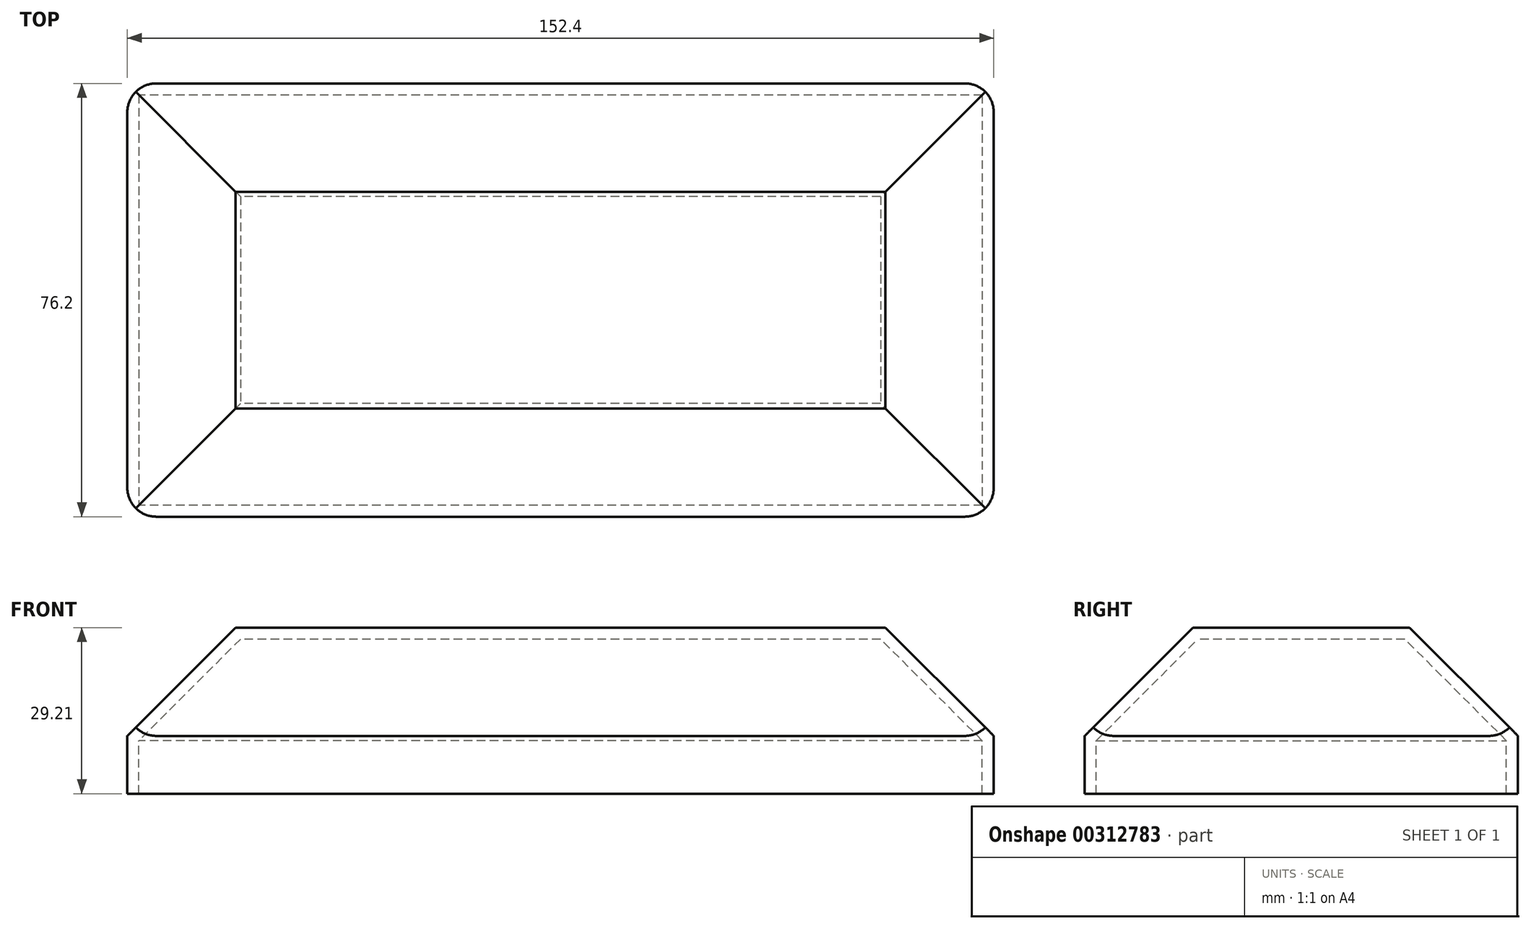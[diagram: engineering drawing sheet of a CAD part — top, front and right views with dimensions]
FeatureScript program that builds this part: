
annotation { "Feature Type Name" : "Feature", "Feature Type Description" : "" }
export const myFeature = defineFeature(function(context is Context, id is Id, definition is map)
    precondition{}
    {
        {
            var Q0;
            Q0=qCreatedBy(makeId("Top.planeOp"),FACE);
            var sketch = newSketch(context, id + "F0", { "sketchPlane" : qUnion([Q0])});
            skLineSegment(sketch, "E0.bottom", {"start": v(0, 0) * mm, "end": v(-152.4, 0) * mm});
            skLineSegment(sketch, "E0.top", {"start": v(0, -76.2) * mm, "end": v(-152.4, -76.2) * mm});
            skLineSegment(sketch, "E0.left", {"start": v(0, 0) * mm, "end": v(0, -76.2) * mm});
            skLineSegment(sketch, "E0.right", {"start": v(-152.4, 0) * mm, "end": v(-152.4, -76.2) * mm});
            skSolve(sketch);
        }
        {
            var Q0;
            Q0=makeQuery(id+"F0.imprint","IMPRINT",FACE,{"disambiguationData":[TD([[makeQuery(id+"F0.imprint","IMPRINT",EDGE,{"derivedFrom":sQuery(id+"F0.wireOp",EDGE,"E0.bottom")}),1.0]])]});
            extrude(context, id + "F1", {"entities" : qUnion([Q0]), "depth" : 19.05 * mm});
        }
        {
            var Q0;
            Q0=makeQuery(id+"F1.opExtrude","CAP_FACE",FACE,{"disambiguationData":[OSD([sQuery(id+"F0.wireOp",EDGE,"E0.bottom"),sQuery(id+"F0.wireOp",EDGE,"E0.top"),sQuery(id+"F0.wireOp",EDGE,"E0.left"),sQuery(id+"F0.wireOp",EDGE,"E0.right")])],"isStart":false});
            chamfer(context, id + "F2", {"entities" : qUnion([Q0]), "width" : 19.05 * mm, "tangentPropagation" : true});
        }
        {
            var Q0;
            Q0=makeQuery(id+"F1.opExtrude","CAP_FACE",FACE,{"disambiguationData":[OSD([sQuery(id+"F0.wireOp",EDGE,"E0.bottom"),sQuery(id+"F0.wireOp",EDGE,"E0.top"),sQuery(id+"F0.wireOp",EDGE,"E0.left"),sQuery(id+"F0.wireOp",EDGE,"E0.right")])],"isStart":true});
            var sketch = newSketch(context, id + "F3", { "sketchPlane" : qUnion([Q0])});
            skLineSegment(sketch, "E1.bottom", {"start": v(0, 0) * mm, "end": v(-152.4, 0) * mm});
            skLineSegment(sketch, "E1.top", {"start": v(0, 76.2) * mm, "end": v(-152.4, 76.2) * mm});
            skLineSegment(sketch, "E1.left", {"start": v(0, 0) * mm, "end": v(0, 76.2) * mm});
            skLineSegment(sketch, "E1.right", {"start": v(-152.4, 0) * mm, "end": v(-152.4, 76.2) * mm});
            skSolve(sketch);
        }
        {
            var Q0;
            Q0=makeQuery(id+"F3.imprint","IMPRINT",FACE,{"disambiguationData":[TD([[makeQuery(id+"F3.imprint","IMPRINT",EDGE,{"derivedFrom":sQuery(id+"F3.wireOp",EDGE,"E1.bottom")}),-1.0]])]});
            extrude(context, id + "F4", {"entities" : qUnion([Q0]), "operationType" : NewBodyOperationType.ADD, "depth" : 10.16 * mm});
        }
        {
            var Q0;
            Q0=makeQuery(id+"F4.opExtrude","CAP_FACE",FACE,{"disambiguationData":[OSD([sQuery(id+"F3.wireOp",EDGE,"E1.bottom"),sQuery(id+"F3.wireOp",EDGE,"E1.top"),sQuery(id+"F3.wireOp",EDGE,"E1.left"),sQuery(id+"F3.wireOp",EDGE,"E1.right")])],"isStart":false});
            shell(context, id + "F5", {"entities" : qUnion([Q0]), "thickness" : 2.03 * mm});
        }
        {
            var Q0;
            Q0=makeQuery(id+"F4.opExtrude","SWEPT_EDGE",EDGE,{"disambiguationData":[OSD([sQuery(id+"F3.wireOp",EDGE,"E1.bottom"),sQuery(id+"F3.wireOp",EDGE,"E1.left")])]});
            var Q1;
            Q1=makeQuery(id+"F4.opExtrude","SWEPT_EDGE",EDGE,{"disambiguationData":[OSD([sQuery(id+"F3.wireOp",EDGE,"E1.bottom"),sQuery(id+"F3.wireOp",EDGE,"E1.right")])]});
            var Q2;
            Q2=makeQuery(id+"F4.opExtrude","SWEPT_EDGE",EDGE,{"disambiguationData":[OSD([sQuery(id+"F3.wireOp",EDGE,"E1.top"),sQuery(id+"F3.wireOp",EDGE,"E1.right")])]});
            var Q3;
            Q3=makeQuery(id+"F4.opExtrude","SWEPT_EDGE",EDGE,{"disambiguationData":[OSD([sQuery(id+"F3.wireOp",EDGE,"E1.top"),sQuery(id+"F3.wireOp",EDGE,"E1.left")])]});
            fillet(context, id + "F6", {"entities" : qUnion([Q0, Q1, Q2, Q3]), "radius" : 5.08 * mm, "tangentPropagation" : true, "allowEdgeOverflow" : false});
        }
    });
